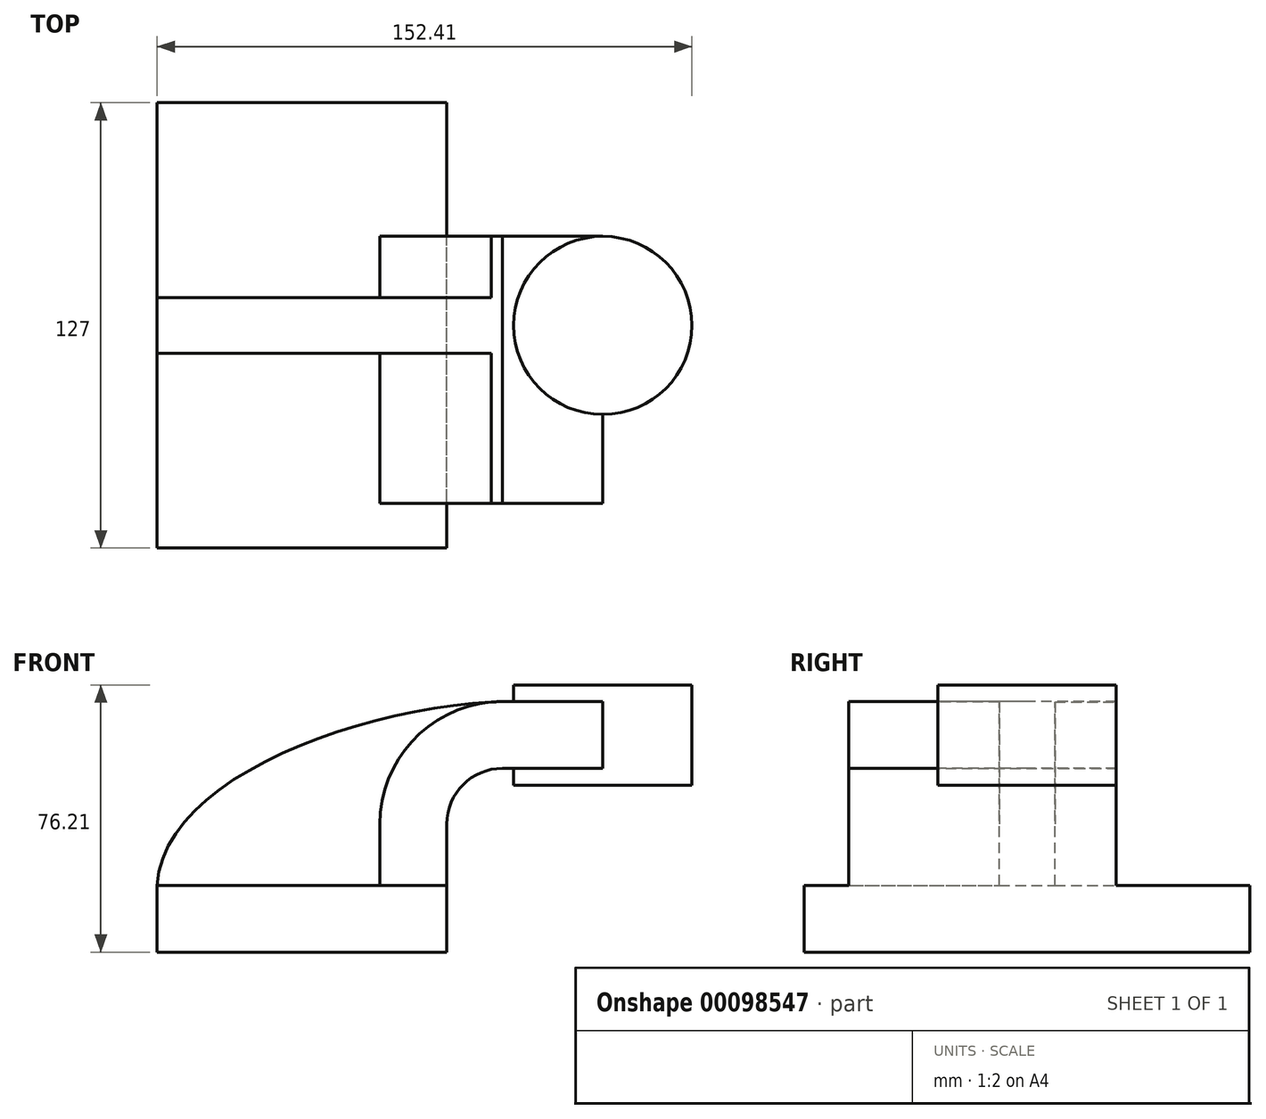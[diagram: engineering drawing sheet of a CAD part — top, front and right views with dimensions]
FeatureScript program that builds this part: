
annotation { "Feature Type Name" : "Feature", "Feature Type Description" : "" }
export const myFeature = defineFeature(function(context is Context, id is Id, definition is map)
    precondition{}
    {
        {
            var Q0;
            Q0=qCreatedBy(makeId("Front.planeOp"),FACE);
            var sketch = newSketch(context, id + "F0", { "sketchPlane" : qUnion([Q0])});
            skLineSegment(sketch, "E0.rect.bottom", {"start": v(-41.28, 9.52) * mm, "end": v(41.28, 9.52) * mm});
            skLineSegment(sketch, "E0.rect.top", {"start": v(-41.28, -9.52) * mm, "end": v(41.28, -9.52) * mm});
            skLineSegment(sketch, "E0.rect.left", {"start": v(-41.28, 9.52) * mm, "end": v(-41.28, -9.52) * mm});
            skLineSegment(sketch, "E0.rect.right", {"start": v(41.28, 9.52) * mm, "end": v(41.28, -9.52) * mm});
            skPoint(sketch, "E0.rect.middle", {"position": v(0, 0) * mm});
            skLineSegment(sketch, "E1", {"start": v(41.28, 9.52) * mm, "end": v(41.28, 27) * mm});
            skArc(sketch, "E2", {"start": v(41.28, 27) * mm, "mid": v(45.92, 38.23) * mm, "end": v(57.15, 42.88) * mm});
            skLineSegment(sketch, "E3", {"start": v(57.15, 42.88) * mm, "end": v(85.72, 42.88) * mm});
            skLineSegment(sketch, "E4.rect.bottom", {"start": v(60.32, 38.1) * mm, "end": v(111.12, 38.1) * mm});
            skLineSegment(sketch, "E4.rect.top", {"start": v(60.32, 66.68) * mm, "end": v(111.12, 66.68) * mm});
            skLineSegment(sketch, "E4.rect.left", {"start": v(60.32, 38.1) * mm, "end": v(60.32, 66.68) * mm});
            skLineSegment(sketch, "E4.rect.right", {"start": v(111.13, 38.1) * mm, "end": v(111.12, 66.68) * mm});
            skPoint(sketch, "E4.rect.middle", {"position": v(85.72, 52.39) * mm});
            skLineSegment(sketch, "E5.0", {"start": v(57.15, 61.93) * mm, "end": v(85.72, 61.93) * mm});
            skArc(sketch, "E5.1", {"start": v(22.23, 27) * mm, "mid": v(32.45, 51.7) * mm, "end": v(57.15, 61.93) * mm});
            skLineSegment(sketch, "E5.2", {"start": v(22.23, 9.52) * mm, "end": v(22.23, 27) * mm});
            skLineSegment(sketch, "E6", {"start": v(85.72, 38.1) * mm, "end": v(85.72, 66.68) * mm});
            skFitSpline(sketch, "E7", {"points": [v(-41.28, 9.53) * mm, v(57.15, 61.93) * mm], "startDerivative": vector(5.2, 92.34) * mm, "endDerivative": vector(120.92, 4.22) * mm});
            skSolve(sketch);
        }
        {
            var Q0;
            Q0=makeQuery(id+"F0.imprint","IMPRINT",FACE,{"disambiguationData":[TD([[makeQuery(id+"F0.imprint","IMPRINT",EDGE,{"derivedFrom":sQuery(id+"F0.wireOp",EDGE,"E0.rect.top")}),1.0]])]});
            extrude(context, id + "F1", {"entities" : qUnion([Q0]), "endBound" : BoundingType.SYMMETRIC, "depth" : 127 * mm});
        }
        {
            var Q0;
            {var subQ9=sQuery(id+"F0.wireOp",EDGE,"E1");Q0=makeQuery(id+"F0.imprint","IMPRINT",FACE,{"disambiguationData":[TD([[makeQuery(id+"F0.imprint","IMPRINT",EDGE,{"derivedFrom":subQ9}),1.0]])]});}
            var Q1;
            {var subQ0=sQuery(id+"F0.wireOp",EDGE,"E6");var subQ1=sQuery(id+"F0.wireOp",EDGE,"E3");var subQ2=makeQuery(id+"F0.imprint","INTERSECT",VERTEX,{"derivedFrom":[subQ1,subQ0]});Q1=makeQuery(id+"F0.imprint","IMPRINT",FACE,{"disambiguationData":[TD([[makeQuery(id+"F0.imprint","IMPRINT",EDGE,{"disambiguationData":[TD([[subQ2,1.0]])],"derivedFrom":subQ1}),1.0]])]});}
            extrude(context, id + "F2", {"entities" : qUnion([Q0, Q1]), "operationType" : NewBodyOperationType.ADD, "endBound" : BoundingType.SYMMETRIC, "depth" : 50.8 * mm});
        }
        {
            var Q0;
            {var subQ3=sQuery(id+"F0.wireOp",EDGE,"E5.2");Q0=makeQuery(id+"F0.imprint","IMPRINT",FACE,{"disambiguationData":[TD([[makeQuery(id+"F0.imprint","IMPRINT",EDGE,{"derivedFrom":subQ3}),1.0]])]});}
            extrude(context, id + "F3", {"entities" : qUnion([Q0]), "operationType" : NewBodyOperationType.ADD, "endBound" : BoundingType.SYMMETRIC, "depth" : 15.88 * mm});
        }
        {
            var Q0;
            {var subQ5=sQuery(id+"F0.wireOp",EDGE,"E4.rect.right");Q0=makeQuery(id+"F0.imprint","IMPRINT",FACE,{"disambiguationData":[TD([[makeQuery(id+"F0.imprint","IMPRINT",EDGE,{"derivedFrom":subQ5}),1.0]])]});}
            var Q1;
            Q1=sQuery(id+"F0.wireOp",EDGE,"E6");
            revolve(context, id + "F4", {"operationType" : NewBodyOperationType.ADD, "entities" : qUnion([Q0]), "axis" : qUnion([Q1]), "revolveType" : RevolveType.FULL});
        }
        {
            var Q0;
            Q0=makeQuery(id+"F2.opExtrude","CAP_FACE",FACE,{"disambiguationData":[OSD([sQuery(id+"F0.wireOp",EDGE,"E0.rect.bottom"),sQuery(id+"F0.wireOp",EDGE,"E1"),sQuery(id+"F0.wireOp",EDGE,"E2"),sQuery(id+"F0.wireOp",EDGE,"E3"),sQuery(id+"F0.wireOp",EDGE,"E5.0"),sQuery(id+"F0.wireOp",EDGE,"E5.1"),sQuery(id+"F0.wireOp",EDGE,"E5.2"),sQuery(id+"F0.wireOp",EDGE,"E6"),sQuery(id+"F0.wireOp",EDGE,"E7")])],"isStart":false});
            extrude(context, id + "F5", {"entities" : qUnion([Q0]), "operationType" : NewBodyOperationType.ADD, "depth" : 25.4 * mm});
        }
    });
